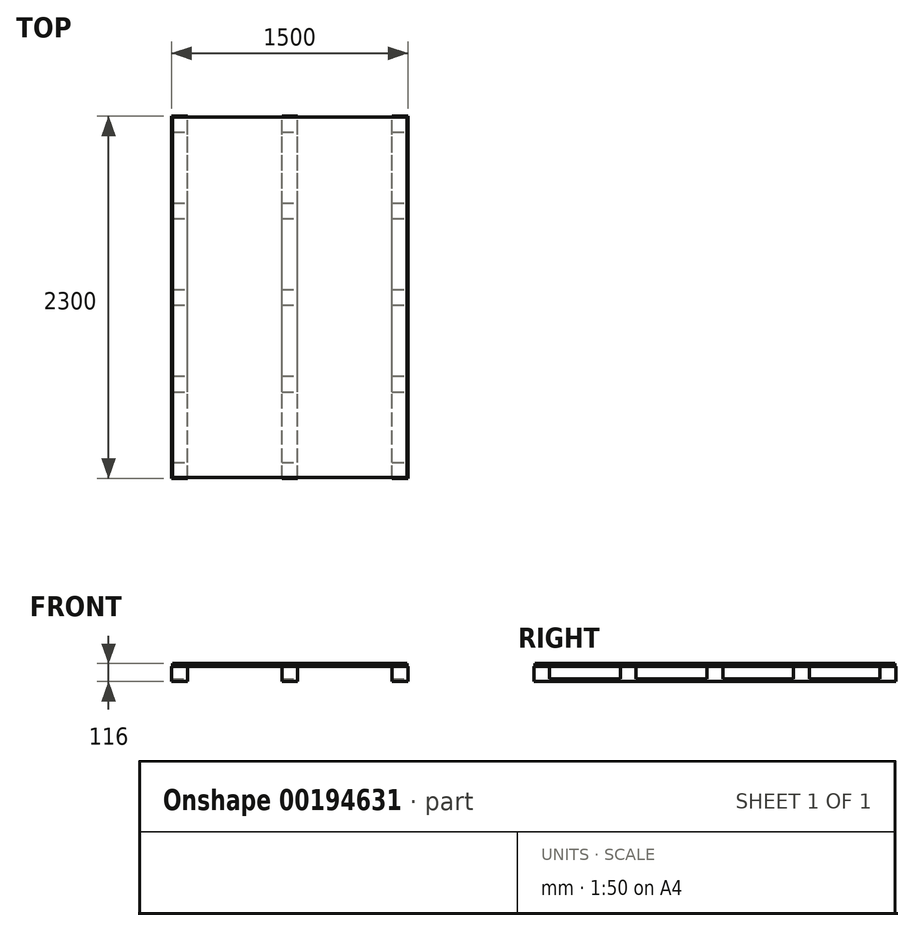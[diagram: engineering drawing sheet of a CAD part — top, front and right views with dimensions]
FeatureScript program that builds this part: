
annotation { "Feature Type Name" : "Feature", "Feature Type Description" : "" }
export const myFeature = defineFeature(function(context is Context, id is Id, definition is map)
    precondition{}
    {
        {
            var Q0;
            Q0=qCreatedBy(makeId("Top.planeOp"),FACE);
            var sketch = newSketch(context, id + "F0", { "sketchPlane" : qUnion([Q0])});
            skLineSegment(sketch, "E0.bottom", {"start": v(744, 1144) * mm, "end": v(-744, 1144) * mm});
            skLineSegment(sketch, "E0.top", {"start": v(744, -1144) * mm, "end": v(-744, -1144) * mm});
            skLineSegment(sketch, "E0.left", {"start": v(744, 1144) * mm, "end": v(744, -1144) * mm});
            skLineSegment(sketch, "E0.right", {"start": v(-744, 1144) * mm, "end": v(-744, -1144) * mm});
            skPoint(sketch, "E0.middle", {"position": v(0, 0) * mm});
            skSolve(sketch);
        }
        {
            var Q0;
            Q0 = qSketchRegion(id + "F0", true);
            extrude(context, id + "F1", {"entities" : qUnion([Q0]), "depth" : 18 * mm});
        }
        {
            var Q0;
            Q0=makeQuery(id+"F1.opExtrude","CAP_FACE",FACE,{"disambiguationData":[OSD([sQuery(id+"F0.wireOp",EDGE,"E0.bottom"),sQuery(id+"F0.wireOp",EDGE,"E0.top"),sQuery(id+"F0.wireOp",EDGE,"E0.left"),sQuery(id+"F0.wireOp",EDGE,"E0.right")])],"isStart":true});
            var sketch = newSketch(context, id + "F2", { "sketchPlane" : qUnion([Q0])});
            skLineSegment(sketch, "E1.bottom", {"start": v(-750, 1150) * mm, "end": v(-650, 1150) * mm});
            skLineSegment(sketch, "E1.top", {"start": v(-750, 1050) * mm, "end": v(-650, 1050) * mm});
            skLineSegment(sketch, "E1.left", {"start": v(-750, 1150) * mm, "end": v(-750, 1050) * mm});
            skLineSegment(sketch, "E1.right", {"start": v(-650, 1150) * mm, "end": v(-650, 1050) * mm});
            skLineSegment(sketch, "E2.0.1.0", {"start": v(-750, 600) * mm, "end": v(-650, 600) * mm});
            skLineSegment(sketch, "E2.0.1.1", {"start": v(-650, 600) * mm, "end": v(-650, 500) * mm});
            skLineSegment(sketch, "E2.0.1.2", {"start": v(-750, 600) * mm, "end": v(-750, 500) * mm});
            skLineSegment(sketch, "E2.0.1.3", {"start": v(-750, 500) * mm, "end": v(-650, 500) * mm});
            skLineSegment(sketch, "E2.0.2.0", {"start": v(-750, 50) * mm, "end": v(-650, 50) * mm});
            skLineSegment(sketch, "E2.0.2.1", {"start": v(-650, 50) * mm, "end": v(-650, -50) * mm});
            skLineSegment(sketch, "E2.0.2.2", {"start": v(-750, 50) * mm, "end": v(-750, -50) * mm});
            skLineSegment(sketch, "E2.0.2.3", {"start": v(-750, -50) * mm, "end": v(-650, -50) * mm});
            skLineSegment(sketch, "E2.0.3.0", {"start": v(-750, -500) * mm, "end": v(-650, -500) * mm});
            skLineSegment(sketch, "E2.0.3.1", {"start": v(-650, -500) * mm, "end": v(-650, -600) * mm});
            skLineSegment(sketch, "E2.0.3.2", {"start": v(-750, -500) * mm, "end": v(-750, -600) * mm});
            skLineSegment(sketch, "E2.0.3.3", {"start": v(-750, -600) * mm, "end": v(-650, -600) * mm});
            skLineSegment(sketch, "E2.0.4.0", {"start": v(-750, -1050) * mm, "end": v(-650, -1050) * mm});
            skLineSegment(sketch, "E2.0.4.1", {"start": v(-650, -1050) * mm, "end": v(-650, -1150) * mm});
            skLineSegment(sketch, "E2.0.4.2", {"start": v(-750, -1050) * mm, "end": v(-750, -1150) * mm});
            skLineSegment(sketch, "E2.0.4.3", {"start": v(-750, -1150) * mm, "end": v(-650, -1150) * mm});
            skLineSegment(sketch, "E2.1.0.0", {"start": v(-50, 1150) * mm, "end": v(50, 1150) * mm});
            skLineSegment(sketch, "E2.1.0.1", {"start": v(50, 1150) * mm, "end": v(50, 1050) * mm});
            skLineSegment(sketch, "E2.1.0.2", {"start": v(-50, 1150) * mm, "end": v(-50, 1050) * mm});
            skLineSegment(sketch, "E2.1.0.3", {"start": v(-50, 1050) * mm, "end": v(50, 1050) * mm});
            skLineSegment(sketch, "E2.1.1.0", {"start": v(-50, 600) * mm, "end": v(50, 600) * mm});
            skLineSegment(sketch, "E2.1.1.1", {"start": v(50, 600) * mm, "end": v(50, 500) * mm});
            skLineSegment(sketch, "E2.1.1.2", {"start": v(-50, 600) * mm, "end": v(-50, 500) * mm});
            skLineSegment(sketch, "E2.1.1.3", {"start": v(-50, 500) * mm, "end": v(50, 500) * mm});
            skLineSegment(sketch, "E2.1.2.0", {"start": v(-50, 50) * mm, "end": v(50, 50) * mm});
            skLineSegment(sketch, "E2.1.2.1", {"start": v(50, 50) * mm, "end": v(50, -50) * mm});
            skLineSegment(sketch, "E2.1.2.2", {"start": v(-50, 50) * mm, "end": v(-50, -50) * mm});
            skLineSegment(sketch, "E2.1.2.3", {"start": v(-50, -50) * mm, "end": v(50, -50) * mm});
            skLineSegment(sketch, "E2.1.3.0", {"start": v(-50, -500) * mm, "end": v(50, -500) * mm});
            skLineSegment(sketch, "E2.1.3.1", {"start": v(50, -500) * mm, "end": v(50, -600) * mm});
            skLineSegment(sketch, "E2.1.3.2", {"start": v(-50, -500) * mm, "end": v(-50, -600) * mm});
            skLineSegment(sketch, "E2.1.3.3", {"start": v(-50, -600) * mm, "end": v(50, -600) * mm});
            skLineSegment(sketch, "E2.1.4.0", {"start": v(-50, -1050) * mm, "end": v(50, -1050) * mm});
            skLineSegment(sketch, "E2.1.4.1", {"start": v(50, -1050) * mm, "end": v(50, -1150) * mm});
            skLineSegment(sketch, "E2.1.4.2", {"start": v(-50, -1050) * mm, "end": v(-50, -1150) * mm});
            skLineSegment(sketch, "E2.1.4.3", {"start": v(-50, -1150) * mm, "end": v(50, -1150) * mm});
            skLineSegment(sketch, "E2.2.0.0", {"start": v(650, 1150) * mm, "end": v(750, 1150) * mm});
            skLineSegment(sketch, "E2.2.0.1", {"start": v(750, 1150) * mm, "end": v(750, 1050) * mm});
            skLineSegment(sketch, "E2.2.0.2", {"start": v(650, 1150) * mm, "end": v(650, 1050) * mm});
            skLineSegment(sketch, "E2.2.0.3", {"start": v(650, 1050) * mm, "end": v(750, 1050) * mm});
            skLineSegment(sketch, "E2.2.1.0", {"start": v(650, 600) * mm, "end": v(750, 600) * mm});
            skLineSegment(sketch, "E2.2.1.1", {"start": v(750, 600) * mm, "end": v(750, 500) * mm});
            skLineSegment(sketch, "E2.2.1.2", {"start": v(650, 600) * mm, "end": v(650, 500) * mm});
            skLineSegment(sketch, "E2.2.1.3", {"start": v(650, 500) * mm, "end": v(750, 500) * mm});
            skLineSegment(sketch, "E2.2.2.0", {"start": v(650, 50) * mm, "end": v(750, 50) * mm});
            skLineSegment(sketch, "E2.2.2.1", {"start": v(750, 50) * mm, "end": v(750, -50) * mm});
            skLineSegment(sketch, "E2.2.2.2", {"start": v(650, 50) * mm, "end": v(650, -50) * mm});
            skLineSegment(sketch, "E2.2.2.3", {"start": v(650, -50) * mm, "end": v(750, -50) * mm});
            skLineSegment(sketch, "E2.2.3.0", {"start": v(650, -500) * mm, "end": v(750, -500) * mm});
            skLineSegment(sketch, "E2.2.3.1", {"start": v(750, -500) * mm, "end": v(750, -600) * mm});
            skLineSegment(sketch, "E2.2.3.2", {"start": v(650, -500) * mm, "end": v(650, -600) * mm});
            skLineSegment(sketch, "E2.2.3.3", {"start": v(650, -600) * mm, "end": v(750, -600) * mm});
            skLineSegment(sketch, "E2.2.4.0", {"start": v(650, -1050) * mm, "end": v(750, -1050) * mm});
            skLineSegment(sketch, "E2.2.4.1", {"start": v(750, -1050) * mm, "end": v(750, -1150) * mm});
            skLineSegment(sketch, "E2.2.4.2", {"start": v(650, -1050) * mm, "end": v(650, -1150) * mm});
            skLineSegment(sketch, "E2.2.4.3", {"start": v(650, -1150) * mm, "end": v(750, -1150) * mm});
            skLineSegment(sketch, "E2.direction1", {"start": v(-750, 1150) * mm, "end": v(-50, 1150) * mm, "construction": true});
            skLineSegment(sketch, "E2.direction2", {"start": v(-750, 1150) * mm, "end": v(-750, 600) * mm, "construction": true});
            skSolve(sketch);
        }
        {
            var Q0;
            Q0 = qSketchRegion(id + "F2", true);
            extrude(context, id + "F3", {"entities" : qUnion([Q0]), "operationType" : NewBodyOperationType.ADD, "depth" : 80 * mm});
        }
        {
            var Q0;
            Q0=makeQuery(id+"F3.opExtrude","CAP_FACE",FACE,{"disambiguationData":[OSD([sQuery(id+"F2.wireOp",EDGE,"E1.bottom"),sQuery(id+"F2.wireOp",EDGE,"E1.top"),sQuery(id+"F2.wireOp",EDGE,"E1.left"),sQuery(id+"F2.wireOp",EDGE,"E1.right")])],"isStart":false});
            var sketch = newSketch(context, id + "F4", { "sketchPlane" : qUnion([Q0])});
            skLineSegment(sketch, "E3.bottom", {"start": v(-750, 1150) * mm, "end": v(-650, 1150) * mm});
            skLineSegment(sketch, "E3.top", {"start": v(-750, -1150) * mm, "end": v(-650, -1150) * mm});
            skLineSegment(sketch, "E3.left", {"start": v(-750, 1150) * mm, "end": v(-750, -1150) * mm});
            skLineSegment(sketch, "E3.right", {"start": v(-650, 1150) * mm, "end": v(-650, -1150) * mm});
            skLineSegment(sketch, "E4.1.0.0", {"start": v(-50, 1150) * mm, "end": v(50, 1150) * mm});
            skLineSegment(sketch, "E4.1.0.1", {"start": v(-50, 1150) * mm, "end": v(-50, -1150) * mm});
            skLineSegment(sketch, "E4.1.0.2", {"start": v(50, 1150) * mm, "end": v(50, -1150) * mm});
            skLineSegment(sketch, "E4.1.0.3", {"start": v(-50, -1150) * mm, "end": v(50, -1150) * mm});
            skLineSegment(sketch, "E4.2.0.0", {"start": v(650, 1150) * mm, "end": v(750, 1150) * mm});
            skLineSegment(sketch, "E4.2.0.1", {"start": v(650, 1150) * mm, "end": v(650, -1150) * mm});
            skLineSegment(sketch, "E4.2.0.2", {"start": v(750, 1150) * mm, "end": v(750, -1150) * mm});
            skLineSegment(sketch, "E4.2.0.3", {"start": v(650, -1150) * mm, "end": v(750, -1150) * mm});
            skLineSegment(sketch, "E4.direction1", {"start": v(-750, 1150) * mm, "end": v(-50, 1150) * mm, "construction": true});
            skSolve(sketch);
        }
        {
            var Q0;
            Q0 = qSketchRegion(id + "F4", true);
            extrude(context, id + "F5", {"entities" : qUnion([Q0]), "operationType" : NewBodyOperationType.ADD, "depth" : 18 * mm});
        }
    });
